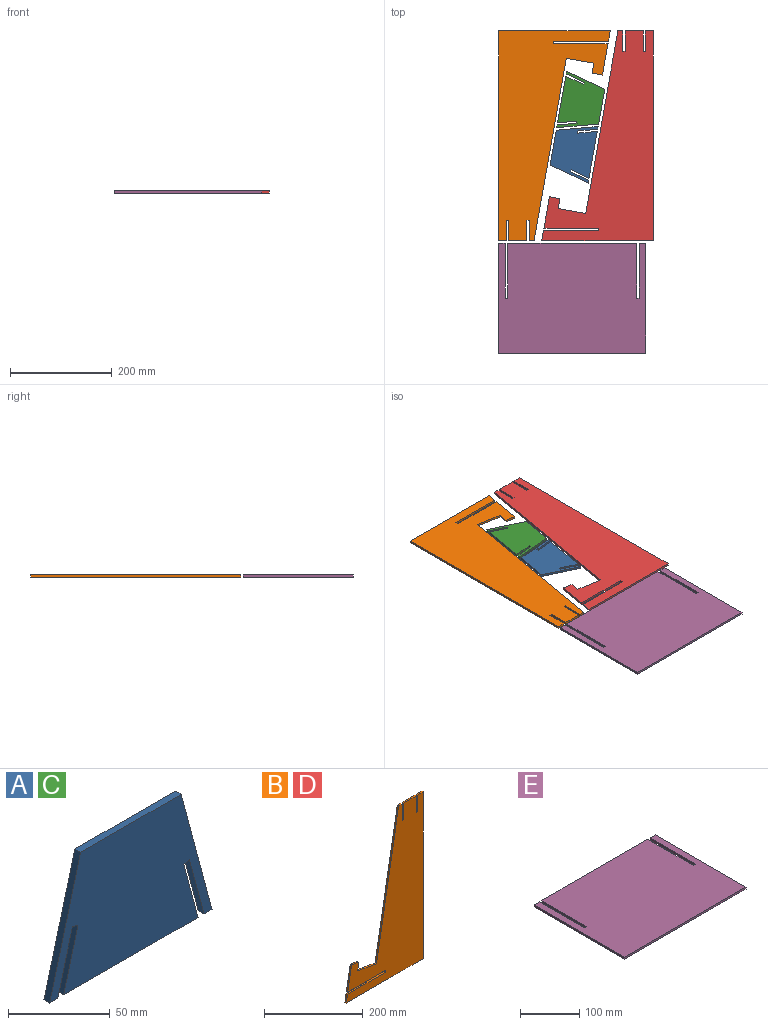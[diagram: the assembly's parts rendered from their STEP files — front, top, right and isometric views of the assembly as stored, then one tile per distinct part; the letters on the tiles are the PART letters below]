
ASSEMBLY  parts=5 mates=4
PART A: 14 faces, bbox 112.9x4x80 mm
  f0: plane 93.46x4mm, normal (0,0,-1), area 373.8mm2, adj f2,f7,f10,f12
  f1: plane 5.56x4mm, normal (0,0,-1), area 22.2mm2, adj f2,f3,f7,f9
  f2: plane 112.87x80mm, normal (0,1,0), area 7004.4mm2, adj f0,f1,f3,f4,f5,f6,f8,f9
  f3: plane 80x21.44mm, normal (0.97,0,0.26), area 331.3mm2, adj f1,f2,f4,f7
  f4: plane 70x4mm, normal (0,0,1), area 280mm2, adj f2,f3,f5,f7
  f5: plane 80x21.44mm, normal (-0.97,0,0.26), area 331.3mm2, adj f2,f4,f6,f7
  f6: plane 5.57x4mm, normal (0,0,-1), area 22.3mm2, adj f2,f5,f7,f13
  f7: plane 112.87x80mm, normal (0,-1,0), area 7004.4mm2, adj f0,f1,f3,f4,f5,f6,f8,f9
  f8: plane 4x3.86mm, normal (0.26,0,-0.97), area 16mm2, adj f2,f7,f9,f10
  f9: plane 38x10.18mm, normal (-0.97,0,-0.26), area 157.4mm2, adj f1,f2,f7,f8
  f10: plane 36.96x9.9mm, normal (0.97,0,0.26), area 153.1mm2, adj f0,f2,f7,f8
  f11: plane 4x3.86mm, normal (-0.26,0,-0.97), area 16mm2, adj f2,f7,f12,f13
  f12: plane 36.96x9.9mm, normal (-0.97,0,0.26), area 153.1mm2, adj f0,f2,f7,f11
  f13: plane 38x10.18mm, normal (0.97,0,-0.26), area 157.4mm2, adj f2,f6,f7,f11
PART B: 22 faces, bbox 220x4x413.5 mm
  f0: plane 36x4mm, normal (0,0,1), area 144mm2, adj f1,f5,f7,f21
  f1: plane 40.59x4mm, normal (1,0,0), area 162.4mm2, adj f0,f2,f5,f7
  f2: plane 4x4mm, normal (0,0,1), area 16mm2, adj f1,f3,f5,f7
  f3: plane 40.59x4mm, normal (-1,0,0), area 162.4mm2, adj f2,f5,f7,f10
  f4: plane 10x4mm, normal (0,0,1), area 40mm2, adj f5,f7,f11,f19
  f5: plane 413.46x220mm, normal (0,-1,0), area 48221.7mm2, adj f0,f1,f2,f3,f4,f6,f8,f9
  f6: plane 20x4mm, normal (-0.98,0,0.17), area 81.2mm2, adj f5,f7,f8,f17
  f7: plane 413.46x220mm, normal (0,1,0), area 48221.7mm2, adj f0,f1,f2,f3,f4,f6,f8,f9
  f8: plane 220x4mm, normal (0,0,-1), area 880mm2, adj f5,f6,f7,f9
  f9: plane 413.46x4mm, normal (1,0,0), area 1653.8mm2, adj f5,f7,f8,f10
  f10: plane 16x4mm, normal (0,0,1), area 64mm2, adj f3,f5,f7,f9
  f11: plane 359.46x63.38mm, normal (-0.98,0,0.17), area 1460mm2, adj f4,f5,f7,f12
  f12: plane 54.16x9.55mm, normal (0.17,0,0.98), area 220mm2, adj f5,f7,f11,f13
  f13: plane 19.7x4mm, normal (0.98,0,-0.17), area 80mm2, adj f5,f7,f12,f14
  f14: plane 20.61x4mm, normal (0.17,0,0.98), area 83.7mm2, adj f5,f7,f13,f15
  f15: plane 61.74x10.89mm, normal (-0.98,0,0.17), area 250.8mm2, adj f5,f7,f14,f18
  f16: plane 5.14x4mm, normal (-1,0,0), area 20.6mm2, adj f5,f7,f17,f18
  f17: plane 108.7x4mm, normal (0,0,1), area 434.8mm2, adj f5,f6,f7,f16
  f18: plane 107.79x4mm, normal (0,0,-1), area 431.2mm2, adj f5,f7,f15,f16
  f19: plane 40.59x4mm, normal (1,0,0), area 162.4mm2, adj f4,f5,f7,f20
  f20: plane 4x4mm, normal (0,0,1), area 16mm2, adj f5,f7,f19,f21
  f21: plane 40.59x4mm, normal (-1,0,0), area 162.4mm2, adj f0,f5,f7,f20
PART C: same geometry as A
PART D: same geometry as B
PART E: 14 faces, bbox 290x216x4 mm
  f0: plane 13.07x4mm, normal (0,1,0), area 52.3mm2, adj f1,f3,f4,f11
  f1: plane 290x216mm, normal (0,0,-1), area 61531.4mm2, adj f0,f2,f4,f5,f6,f7,f8,f9
  f2: plane 253.57x4mm, normal (0,1,0), area 1014.3mm2, adj f1,f3,f8,f12
  f3: plane 290x216mm, normal (0,0,1), area 61531.4mm2, adj f0,f2,f4,f5,f6,f7,f8,f9
  f4: plane 216x4mm, normal (-1,0,0), area 864mm2, adj f0,f1,f3,f6
  f5: plane 216x4mm, normal (1,0,0), area 864mm2, adj f1,f3,f6,f7
  f6: plane 290x4mm, normal (0,-1,0), area 1160mm2, adj f1,f3,f4,f5
  f7: plane 13.07x4mm, normal (0,1,0), area 52.3mm2, adj f1,f3,f5,f10
  f8: plane 107.87x4mm, normal (1,0,0), area 431.5mm2, adj f1,f2,f3,f9
  f9: plane 5.14x4mm, normal (-0.02,1,0), area 20.6mm2, adj f1,f3,f8,f10
  f10: plane 107.75x4mm, normal (-1,0,0), area 431mm2, adj f1,f3,f7,f9
  f11: plane 107.75x4mm, normal (1,0,0), area 431mm2, adj f0,f1,f3,f13
  f12: plane 107.87x4mm, normal (-1,0,0), area 431.5mm2, adj f1,f2,f3,f13
  f13: plane 5.14x4mm, normal (0.02,1,0), area 20.6mm2, adj f1,f3,f11,f12
PLACE A rot(axis=(-0.64,-0.54,0.54),114.4deg) t=(329.96,406.27,242.08)mm
PLACE B rot(axis=(0,-0.71,0.71),180deg) t=(606.93,352.55,242.08)mm
PLACE C rot(axis=(-0.51,0.61,-0.61),125.9deg) t=(69.85,411.91,242.08)mm
PLACE D rot(axis=(-1,0,0),90deg) t=(-212.49,431.17,242.08)mm
PLACE E rot(axis=(-0.2,-0.94,-0.28),0deg) t=(259.88,180.13,470.8)mm fixed
MATE fastened E.f3 <-> D.f5  axis (0,0,1) through (334.72,180.13,246.08)mm
MATE fastened E.f3 <-> B.f5  axis (0,0,1) through (44.72,180.13,246.08)mm
MATE fastened C.f7 <-> B.f5  axis (0,0,1) through (178.68,519.1,246.08)mm
MATE fastened A.f7 <-> C.f7  axis (0,0,1) through (240.72,410.24,246.08)mm
